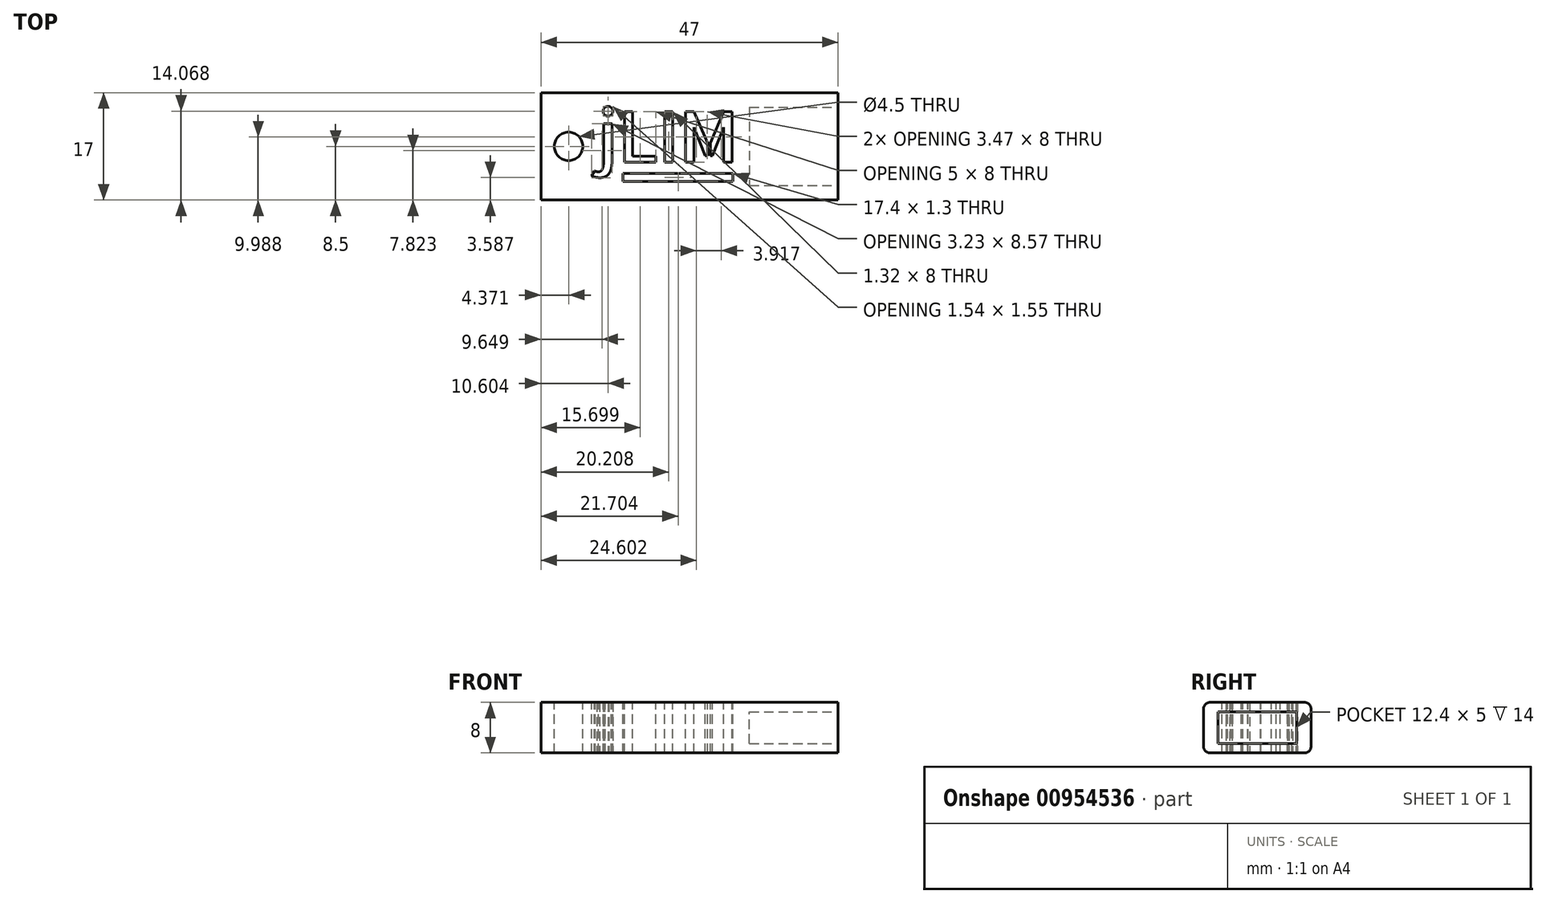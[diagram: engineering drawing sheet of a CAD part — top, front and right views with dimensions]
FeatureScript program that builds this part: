
annotation { "Feature Type Name" : "Feature", "Feature Type Description" : "" }
export const myFeature = defineFeature(function(context is Context, id is Id, definition is map)
    precondition{}
    {
        {
            var Q0;
            Q0=qCreatedBy(makeId("Front.planeOp"),FACE);
            var sketch = newSketch(context, id + "F0", { "sketchPlane" : qUnion([Q0])});
            skLineSegment(sketch, "E0.bottom", {"start": v(7.5, -4) * mm, "end": v(-7.5, -4) * mm});
            skLineSegment(sketch, "E0.top", {"start": v(7.5, 4) * mm, "end": v(-7.5, 4) * mm});
            skLineSegment(sketch, "E0.left", {"start": v(8.5, -3) * mm, "end": v(8.5, 3) * mm});
            skLineSegment(sketch, "E0.right", {"start": v(-8.5, -3) * mm, "end": v(-8.5, 3) * mm});
            skPoint(sketch, "E0.middle", {"position": v(0, 0) * mm});
            skPoint(sketch, "E1.visualSharp", {"position": v(-8.5, 4) * mm});
            skArc(sketch, "E1.filletArc", {"start": v(-7.5, 4) * mm, "mid": v(-8.2, 3.7) * mm, "end": v(-8.5, 3) * mm});
            skPoint(sketch, "E2.visualSharp", {"position": v(8.5, 4) * mm});
            skArc(sketch, "E2.filletArc", {"start": v(8.5, 3) * mm, "mid": v(8.2, 3.7) * mm, "end": v(7.5, 4) * mm});
            skPoint(sketch, "E3.visualSharp", {"position": v(-8.5, -4) * mm});
            skArc(sketch, "E3.filletArc", {"start": v(-8.5, -3) * mm, "mid": v(-8.2, -3.7) * mm, "end": v(-7.5, -4) * mm});
            skPoint(sketch, "E4.visualSharp", {"position": v(8.5, -4) * mm});
            skArc(sketch, "E4.filletArc", {"start": v(7.5, -4) * mm, "mid": v(8.2, -3.7) * mm, "end": v(8.5, -3) * mm});
            skSolve(sketch);
        }
        {
            var Q0;
            Q0=makeQuery(id+"F0.imprint","IMPRINT",FACE,{"disambiguationData":[TD([[makeQuery(id+"F0.imprint","IMPRINT",EDGE,{"derivedFrom":sQuery(id+"F0.wireOp",EDGE,"E0.bottom")}),-1.0]])]});
            extrude(context, id + "F1", {"entities" : qUnion([Q0]), "depth" : 47 * mm, "offsetDistance" : 25 * mm});
        }
        {
            var Q0;
            Q0=makeQuery(id+"F1.opExtrude","CAP_FACE",FACE,{"disambiguationData":[OSD([sQuery(id+"F0.wireOp",EDGE,"E0.bottom"),sQuery(id+"F0.wireOp",EDGE,"E0.top"),sQuery(id+"F0.wireOp",EDGE,"E0.left"),sQuery(id+"F0.wireOp",EDGE,"E0.right"),sQuery(id+"F0.wireOp",EDGE,"E1.filletArc"),sQuery(id+"F0.wireOp",EDGE,"E2.filletArc"),sQuery(id+"F0.wireOp",EDGE,"E3.filletArc"),sQuery(id+"F0.wireOp",EDGE,"E4.filletArc")])],"isStart":false});
            var sketch = newSketch(context, id + "F2", { "sketchPlane" : qUnion([Q0])});
            skLineSegment(sketch, "E5.bottom", {"start": v(6.2, -2.5) * mm, "end": v(-6.2, -2.5) * mm});
            skLineSegment(sketch, "E5.top", {"start": v(6.2, 2.5) * mm, "end": v(-6.2, 2.5) * mm});
            skLineSegment(sketch, "E5.left", {"start": v(6.2, -2.5) * mm, "end": v(6.2, 2.5) * mm});
            skLineSegment(sketch, "E5.right", {"start": v(-6.2, -2.5) * mm, "end": v(-6.2, 2.5) * mm});
            skPoint(sketch, "E5.middle", {"position": v(0, 0) * mm});
            skSolve(sketch);
        }
        {
            var Q0;
            Q0=makeQuery(id+"F2.imprint","IMPRINT",FACE,{"disambiguationData":[TD([[makeQuery(id+"F2.imprint","IMPRINT",EDGE,{"derivedFrom":sQuery(id+"F2.wireOp",EDGE,"E5.bottom")}),-1.0]])]});
            extrude(context, id + "F3", {"entities" : qUnion([Q0]), "operationType" : NewBodyOperationType.REMOVE, "oppositeDirection" : true, "depth" : 14 * mm, "offsetDistance" : 25 * mm});
        }
        {
            var Q0;
            Q0=makeQuery(id+"F1.opExtrude","SWEPT_BODY",BODY,{"disambiguationData":[OSD([sQuery(id+"F0.wireOp",EDGE,"E0.bottom"),sQuery(id+"F0.wireOp",EDGE,"E0.top"),sQuery(id+"F0.wireOp",EDGE,"E0.left"),sQuery(id+"F0.wireOp",EDGE,"E0.right"),sQuery(id+"F0.wireOp",EDGE,"E1.filletArc"),sQuery(id+"F0.wireOp",EDGE,"E2.filletArc"),sQuery(id+"F0.wireOp",EDGE,"E3.filletArc"),sQuery(id+"F0.wireOp",EDGE,"E4.filletArc")])]});
            var Q1;
            Q1=makeQuery(id+"F1.opExtrude","CAP_EDGE",EDGE,{"disambiguationData":[OSD([sQuery(id+"F0.wireOp",EDGE,"E0.left")])],"isStart":true});
            transform(context, id + "F4", {"entities" : qUnion([Q0]), "transformType" : TransformType.ROTATION, "transformAxis" : qUnion([Q1]), "angle" : 90 * degree, "makeCopy" : false});
        }
        {
            var Q0;
            Q0=makeQuery(id+"F1.opExtrude","SWEPT_FACE",FACE,{"disambiguationData":[OSD([sQuery(id+"F0.wireOp",EDGE,"E0.top")])]});
            var sketch = newSketch(context, id + "F5", { "sketchPlane" : qUnion([Q0])});
            skText(sketch, "E6", { "text": "jLIM", "fontName": "AllertaStencil-Regular.ttf"});
            skCircle(sketch, "E7", {"center": v(12.87, -8.5) * mm, "radius": 2.25 * mm});
            skPoint(sketch, "E7.centerSnap0", {"position": v(8.5, -8.5) * mm});
            skLineSegment(sketch, "E8.bottom", {"start": v(21.5, -12.76) * mm, "end": v(38.9, -12.76) * mm});
            skLineSegment(sketch, "E8.top", {"start": v(21.5, -14.06) * mm, "end": v(38.9, -14.06) * mm});
            skLineSegment(sketch, "E8.left", {"start": v(21.5, -12.76) * mm, "end": v(21.5, -14.06) * mm});
            skLineSegment(sketch, "E8.right", {"start": v(38.9, -12.76) * mm, "end": v(38.9, -14.06) * mm});
            const initialGuessF5  = {"E6": [0.01714, -0.01101, 1, 0, 0.008]};
            skSetInitialGuess(sketch, initialGuessF5);
            skSolve(sketch);
        }
        {
            var Q0;
            Q0 = qSketchRegion(id + "F5", true);
            extrude(context, id + "F6", {"entities" : qUnion([Q0]), "operationType" : NewBodyOperationType.REMOVE, "oppositeDirection" : true, "depth" : 10 * mm, "offsetDistance" : 25 * mm});
        }
    });
